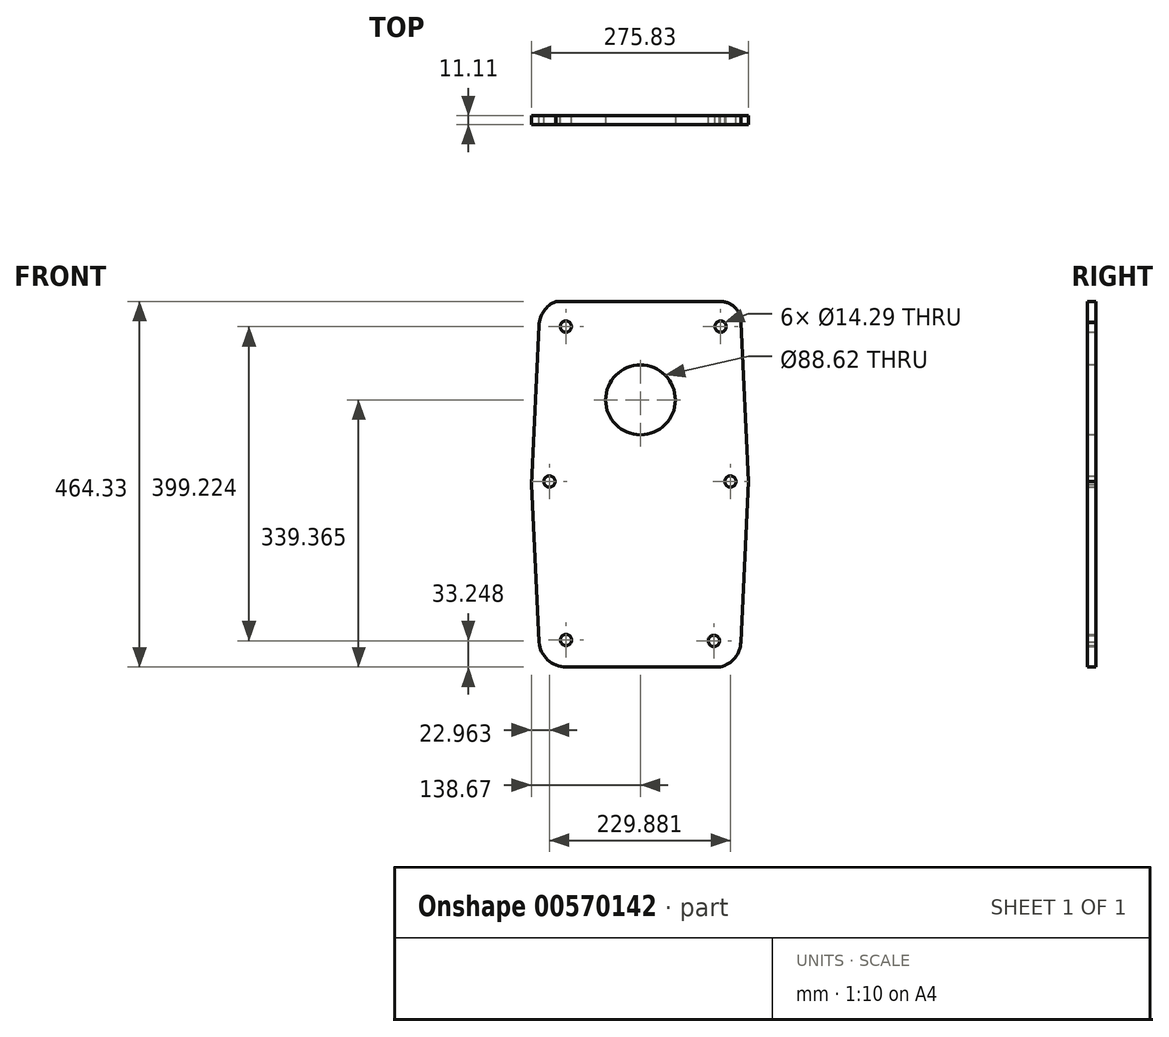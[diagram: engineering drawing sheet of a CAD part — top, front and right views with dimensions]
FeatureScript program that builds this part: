
annotation { "Feature Type Name" : "Feature", "Feature Type Description" : "" }
export const myFeature = defineFeature(function(context is Context, id is Id, definition is map)
    precondition{}
    {
        {
            var Q0;
            Q0=qCreatedBy(makeId("Front.planeOp"),FACE);
            var sketch = newSketch(context, id + "F0", { "sketchPlane" : qUnion([Q0])});
            skLineSegment(sketch, "E0.bottom", {"start": v(101.71, 219.27) * mm, "end": v(-107.57, 219.27) * mm});
            skPoint(sketch, "E0.middle", {"position": v(-0.67, -9.33) * mm});
            skLineSegment(sketch, "E1", {"start": v(-129.1, 189.04) * mm, "end": v(-138.67, -12.96) * mm});
            skLineSegment(sketch, "E2", {"start": v(-138.67, -12.96) * mm, "end": v(-128.86, -213.44) * mm});
            skLineSegment(sketch, "E3", {"start": v(127.6, 192.66) * mm, "end": v(137.16, -9.33) * mm});
            skLineSegment(sketch, "E4", {"start": v(137.16, -9.33) * mm, "end": v(127.5, -213.44) * mm});
            skPoint(sketch, "E5.orphan", {"position": v(-127.67, -237.93) * mm});
            skPoint(sketch, "E6.orphan", {"position": v(126.33, -237.93) * mm});
            skPoint(sketch, "E7.start.orphan", {"position": v(-126.45, 96.17) * mm});
            skPoint(sketch, "E8.start.orphan", {"position": v(127.55, 96.17) * mm});
            skPoint(sketch, "E9.end.orphan", {"position": v(-73.87, 47.55) * mm});
            skPoint(sketch, "E9.start.orphan", {"position": v(74.98, 47.55) * mm});
            skPoint(sketch, "E10.start.orphan", {"position": v(-128.02, 96.5) * mm});
            skPoint(sketch, "E11.start.orphan", {"position": v(125.98, 96.5) * mm});
            skPoint(sketch, "E12.end.orphan", {"position": v(-75.44, 47.89) * mm});
            skPoint(sketch, "E12.start.orphan", {"position": v(73.41, 47.89) * mm});
            skPoint(sketch, "E13.center.orphan", {"position": v(-1.02, 96.5) * mm});
            skPoint(sketch, "E14.orphan", {"position": v(-127.67, 219.27) * mm});
            skPoint(sketch, "E15.orphan", {"position": v(126.33, 219.27) * mm});
            skArc(sketch, "E16", {"start": v(-107.57, 219.27) * mm, "mid": v(-122.77, 207.32) * mm, "end": v(-129.1, 189.04) * mm});
            skArc(sketch, "E17", {"start": v(127.6, 192.66) * mm, "mid": v(120.27, 211.43) * mm, "end": v(101.71, 219.27) * mm});
            skArc(sketch, "E18", {"start": v(101.71, -245.06) * mm, "mid": v(119.81, -233.5) * mm, "end": v(127.5, -213.44) * mm});
            skLineSegment(sketch, "E19", {"start": v(101.71, -245.06) * mm, "end": v(-94.65, -245.06) * mm});
            skArc(sketch, "E20", {"start": v(-128.86, -213.44) * mm, "mid": v(-117.95, -235.94) * mm, "end": v(-94.65, -245.06) * mm});
            skCircle(sketch, "E21", {"center": v(-94.82, 187.41) * mm, "radius": 7.14 * mm});
            skCircle(sketch, "E22", {"center": v(101.71, 187.41) * mm, "radius": 7.14 * mm});
            skCircle(sketch, "E23", {"center": v(-94.65, -210.74) * mm, "radius": 7.14 * mm});
            skCircle(sketch, "E24", {"center": v(93.22, -211.81) * mm, "radius": 7.14 * mm});
            skCircle(sketch, "E25", {"center": v(114.17, -9.33) * mm, "radius": 7.14 * mm});
            skCircle(sketch, "E26", {"center": v(-115.7, -9.33) * mm, "radius": 7.14 * mm});
            skSolve(sketch);
        }
        {
            var Q0;
            Q0=makeQuery(id+"F0.imprint","IMPRINT",FACE,{"disambiguationData":[TD([[makeQuery(id+"F0.imprint","IMPRINT",EDGE,{"derivedFrom":sQuery(id+"F0.wireOp",EDGE,"E0.bottom")}),1.0]])]});
            extrude(context, id + "F1", {"entities" : qUnion([Q0]), "depth" : 11.1 * mm, "offsetDistance" : 25.4 * mm});
        }
        {
            var Q0;
            Q0=makeQuery(id+"F1.opExtrude","CAP_FACE",FACE,{"disambiguationData":[OSD([sQuery(id+"F0.wireOp",EDGE,"E0.bottom"),sQuery(id+"F0.wireOp",EDGE,"E1"),sQuery(id+"F0.wireOp",EDGE,"E2"),sQuery(id+"F0.wireOp",EDGE,"E3"),sQuery(id+"F0.wireOp",EDGE,"E4"),sQuery(id+"F0.wireOp",EDGE,"E16"),sQuery(id+"F0.wireOp",EDGE,"E17"),sQuery(id+"F0.wireOp",EDGE,"E18"),sQuery(id+"F0.wireOp",EDGE,"E19"),sQuery(id+"F0.wireOp",EDGE,"E20"),sQuery(id+"F0.wireOp",EDGE,"E21"),sQuery(id+"F0.wireOp",EDGE,"E22"),sQuery(id+"F0.wireOp",EDGE,"E23"),sQuery(id+"F0.wireOp",EDGE,"E24"),sQuery(id+"F0.wireOp",EDGE,"E25"),sQuery(id+"F0.wireOp",EDGE,"E26")])],"isStart":false});
            var sketch = newSketch(context, id + "F2", { "sketchPlane" : qUnion([Q0])});
            skCircle(sketch, "E27", {"center": v(0, 94.3) * mm, "radius": 44.31 * mm});
            skSolve(sketch);
        }
        {
            var Q0;
            Q0=makeQuery(id+"F2.imprint","IMPRINT",FACE,{"disambiguationData":[TD([[makeQuery(id+"F2.imprint","IMPRINT",EDGE,{"derivedFrom":sQuery(id+"F2.wireOp",EDGE,"E27")}),1.0]])]});
            extrude(context, id + "F3", {"entities" : qUnion([Q0]), "operationType" : NewBodyOperationType.REMOVE, "endBound" : BoundingType.THROUGH_ALL, "oppositeDirection" : true, "depth" : 25.4 * mm, "offsetDistance" : 25.4 * mm});
        }
    });
